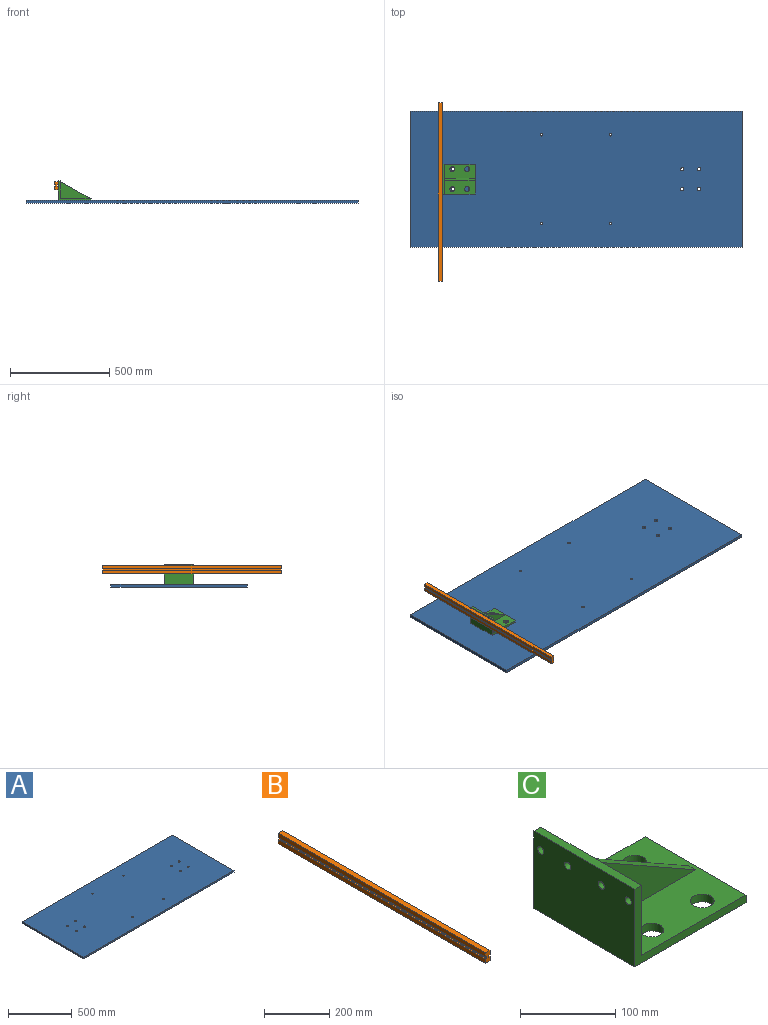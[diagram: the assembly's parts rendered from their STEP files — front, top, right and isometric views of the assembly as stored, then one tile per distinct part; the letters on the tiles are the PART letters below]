
ASSEMBLY  parts=3 mates=2
PART A: 18 faces, bbox 1670x685x15 mm
  f0: plane 1670x15mm, normal (0,1,0), area 25050mm2, adj f1,f5,f16,f17
  f1: plane 685x15mm, normal (-1,0,0), area 10275mm2, adj f0,f2,f16,f17
  f2: plane 1670x15mm, normal (0,-1,0), area 25050mm2, adj f1,f5,f16,f17
  f3: cylinder r=8mm len=16mm, axis (0,0,-1), area 754mm2, adj f16,f17
  f4: cylinder r=6mm len=15mm, axis (0,0,-1), area 565.5mm2, adj f16,f17
  f5: plane 685x15mm, normal (1,0,0), area 10275mm2, adj f0,f2,f16,f17
  f6: cylinder r=8mm len=16mm, axis (0,0,-1), area 754mm2, adj f16,f17
  f7: cylinder r=6mm len=15mm, axis (0,0,-1), area 565.5mm2, adj f16,f17
  f8: cylinder r=8mm len=16mm, axis (0,0,-1), area 754mm2, adj f16,f17
  f9: cylinder r=8mm len=16mm, axis (0,0,-1), area 754mm2, adj f16,f17
  f10: cylinder r=6mm len=15mm, axis (0,0,-1), area 565.5mm2, adj f16,f17
  f11: cylinder r=6mm len=15mm, axis (0,0,-1), area 565.5mm2, adj f16,f17
  f12: cylinder r=8mm len=16mm, axis (0,0,-1), area 754mm2, adj f16,f17
  f13: cylinder r=8mm len=16mm, axis (0,0,-1), area 754mm2, adj f16,f17
  f14: cylinder r=8mm len=16mm, axis (0,0,-1), area 754mm2, adj f16,f17
  f15: cylinder r=8mm len=16mm, axis (0,0,-1), area 754mm2, adj f16,f17
  f16: plane 1670x685mm, normal (0,0,1), area 1141889.1mm2, adj f0,f1,f2,f3,f4,f5,f6,f7
  f17: plane 1670x685mm, normal (0,0,-1), area 1141889.1mm2, adj f0,f1,f2,f3,f4,f5,f6,f7
PART B: 14 faces, bbox 20x900x40 mm
  f0: plane 900x16mm, normal (1,0,0), area 14400mm2, adj f1,f11,f12,f13
  f1: plane 900x20mm, normal (0,0,1), area 18000mm2, adj f0,f2,f12,f13
  f2: plane 900x16mm, normal (-1,0,0), area 14400mm2, adj f1,f3,f12,f13
  f3: plane 900x5mm, normal (0,0,-1), area 4500mm2, adj f2,f4,f12,f13
  f4: plane 900x8mm, normal (-1,0,0), area 7200mm2, adj f3,f5,f12,f13
  f5: plane 900x5mm, normal (0,0,1), area 4500mm2, adj f4,f6,f12,f13
  f6: plane 900x16mm, normal (-1,0,0), area 14400mm2, adj f5,f7,f12,f13
  f7: plane 900x20mm, normal (0,0,-1), area 18000mm2, adj f6,f8,f12,f13
  f8: plane 900x16mm, normal (1,0,0), area 14400mm2, adj f7,f9,f12,f13
  f9: plane 900x5mm, normal (0,0,1), area 4500mm2, adj f8,f10,f12,f13
  f10: plane 900x8mm, normal (1,0,0), area 7200mm2, adj f9,f11,f12,f13
  f11: plane 900x5mm, normal (0,0,-1), area 4500mm2, adj f0,f10,f12,f13
  f12: plane 40x20mm, normal (0,-1,0), area 720mm2, adj f0,f1,f2,f3,f4,f5,f6,f7
  f13: plane 40x20mm, normal (0,1,0), area 720mm2, adj f0,f1,f2,f3,f4,f5,f6,f7
PART C: 19 faces, bbox 165x150x100 mm
  f0: plane 155x150mm, normal (0,0,1), area 19786.5mm2, adj f2,f5,f6,f7,f8,f9,f10,f15
  f1: plane 165x150mm, normal (0,0,-1), area 22786.5mm2, adj f3,f5,f6,f7,f15,f16,f17,f18
  f2: plane 150x90mm, normal (1,0,0), area 12395.5mm2, adj f0,f4,f6,f7,f8,f9,f10,f11
  f3: plane 150x100mm, normal (-1,0,0), area 14745.5mm2, adj f1,f4,f6,f7,f11,f12,f13,f14
  f4: plane 150x10mm, normal (0,0,1), area 1500mm2, adj f2,f3,f6,f7
  f5: plane 150x10mm, normal (1,0,0), area 1500mm2, adj f0,f1,f6,f7
  f6: plane 165x100mm, normal (0,-1,0), area 2550mm2, adj f0,f1,f2,f3,f4,f5
  f7: plane 165x100mm, normal (0,1,0), area 2550mm2, adj f0,f1,f2,f3,f4,f5
  f8: plane 150x85mm, normal (0.49,0,0.87), area 1724.1mm2, adj f0,f2,f9,f10
  f9: plane 150x85mm, normal (0,-1,0), area 6375mm2, adj f0,f2,f8
  f10: plane 150x85mm, normal (0,1,0), area 6375mm2, adj f0,f2,f8
  f11: cylinder r=4.5mm len=10mm, axis (1,0,0), area 282.7mm2, adj f2,f3
  f12: cylinder r=4.5mm len=10mm, axis (1,0,0), area 282.7mm2, adj f2,f3
  f13: cylinder r=4.5mm len=10mm, axis (1,0,0), area 282.7mm2, adj f2,f3
  f14: cylinder r=4.5mm len=10mm, axis (1,0,0), area 282.7mm2, adj f2,f3
  f15: cylinder r=12.5mm len=25mm, axis (0,0,1), area 785.4mm2, adj f0,f1
  f16: cylinder r=12.5mm len=25mm, axis (0,0,1), area 785.4mm2, adj f0,f1
  f17: cylinder r=12.5mm len=25mm, axis (0,0,1), area 785.4mm2, adj f0,f1
  f18: cylinder r=12.5mm len=25mm, axis (0,0,1), area 785.4mm2, adj f0,f1
PLACE A at identity fixed
PLACE B rot(axis=(-1,0,0),0deg) t=(-682.31,-115,90)mm
PLACE C t=(-662.31,0,25)mm
MATE pin_slot A.f6 <-> C.f15  axis (0,0,-1) through (-619,50,15)mm
MATE pin_slot C.f14 <-> B.f0  axis (-1,0,0) through (-672.31,-65,95)mm
